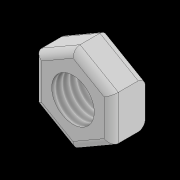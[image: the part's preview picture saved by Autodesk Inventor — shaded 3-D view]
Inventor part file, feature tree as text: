
AUTODESK INVENTOR PART (.ipt)
format: ipt  version: 2022.2 (Build 262287010, 287A)  size: 111,616 bytes
history: native  units: mm
features: extrude x1, thread x1, fillet x1, sketch x1
ambient origin geometry x8: Origin, YZ Plane, XZ Plane, XY Plane, X Axis, Y Axis, Z Axis, Center Point
bodies: Solid1 (feature_tree)
feature tree (4):
  extrude  "Extrusion1"  Depth=1.5mm
  thread  "Thread1"  [1 undecoded]
  fillet  "Fillet1"  [1 undecoded]
  sketch  "Sketch1"  dims[d0=5.4mm d1=1.5mm d2=2.4mm d3=0.0mm d4=2.4mm d5=0.0mm d6=0.5mm]
note: 2 required parameter values undecoded (feature->parameter linkage not recoverable at this tier; creation-order binding heuristic only, values carry confidence <= 0.55)
